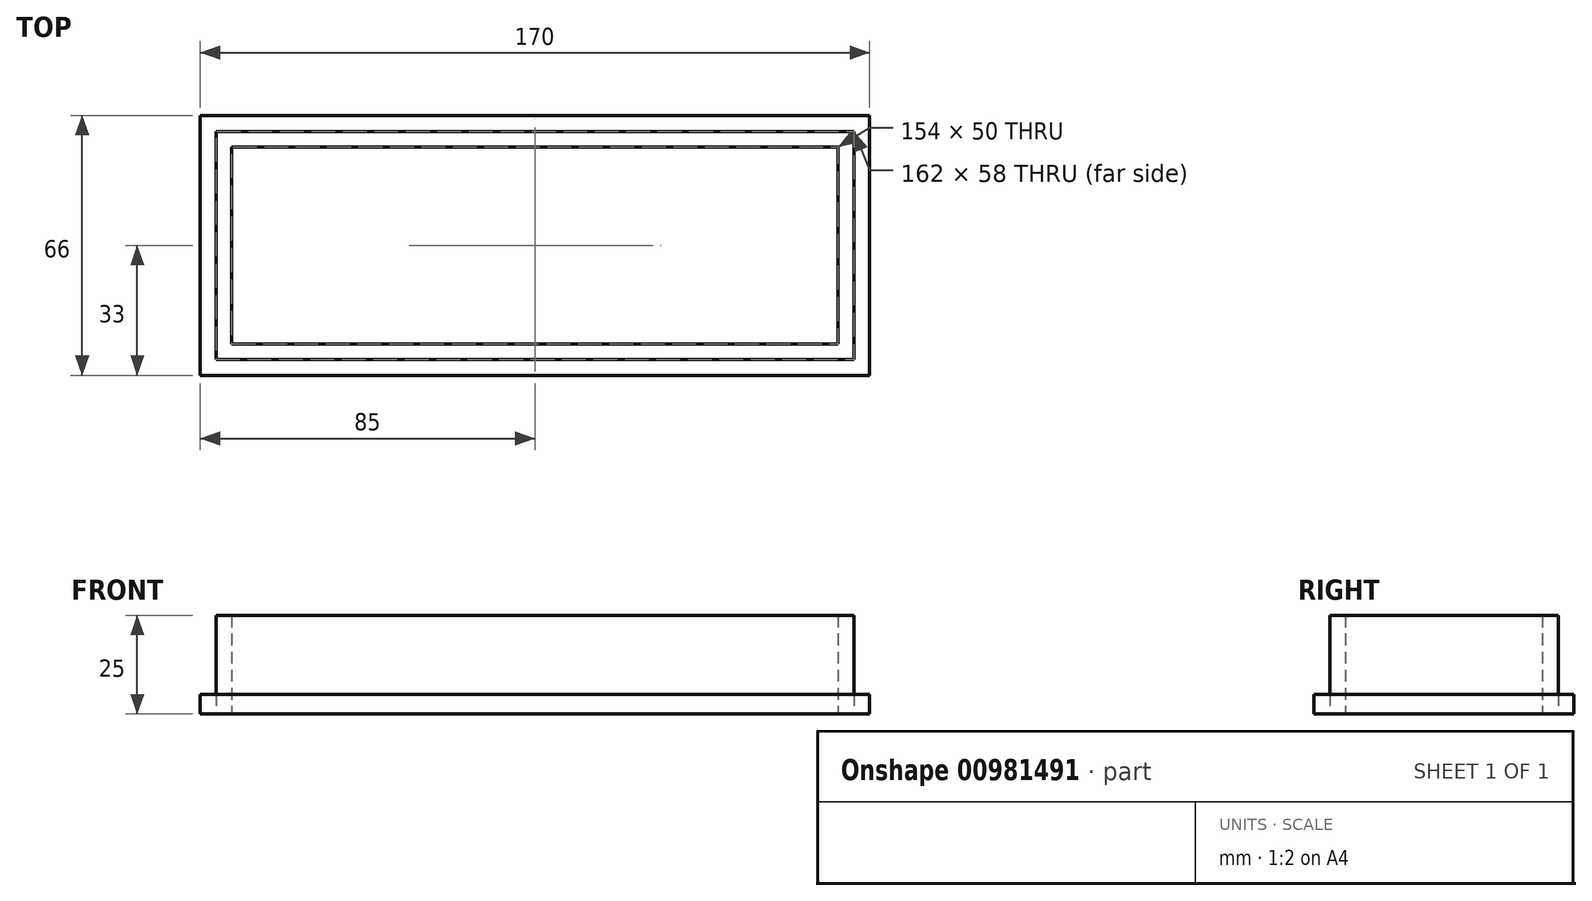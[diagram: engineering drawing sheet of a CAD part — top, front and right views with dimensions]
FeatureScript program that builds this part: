
annotation { "Feature Type Name" : "Feature", "Feature Type Description" : "" }
export const myFeature = defineFeature(function(context is Context, id is Id, definition is map)
    precondition{}
    {
        {
            var Q0;
            Q0=qCreatedBy(makeId("Top.planeOp"),FACE);
            var sketch = newSketch(context, id + "F0", { "sketchPlane" : qUnion([Q0])});
            skLineSegment(sketch, "E0.bottom", {"start": v(-85, 33) * mm, "end": v(85, 33) * mm});
            skLineSegment(sketch, "E0.top", {"start": v(-85, -33) * mm, "end": v(85, -33) * mm});
            skLineSegment(sketch, "E0.left", {"start": v(-85, 33) * mm, "end": v(-85, -33) * mm});
            skLineSegment(sketch, "E0.right", {"start": v(85, 33) * mm, "end": v(85, -33) * mm});
            skLineSegment(sketch, "E1.bottom", {"start": v(81, 29) * mm, "end": v(-81, 29) * mm});
            skLineSegment(sketch, "E1.top", {"start": v(81, -29) * mm, "end": v(-81, -29) * mm});
            skLineSegment(sketch, "E1.left", {"start": v(81, 29) * mm, "end": v(81, -29) * mm});
            skLineSegment(sketch, "E1.right", {"start": v(-81, 29) * mm, "end": v(-81, -29) * mm});
            skPoint(sketch, "E2", {"position": v(-81, 0) * mm});
            skPoint(sketch, "E3", {"position": v(-85, 0) * mm});
            skLineSegment(sketch, "E4", {"start": v(-142.94, 0) * mm, "end": v(129.94, 0) * mm, "construction": true});
            skLineSegment(sketch, "E5.bottom", {"start": v(-77, 25) * mm, "end": v(77, 25) * mm});
            skLineSegment(sketch, "E5.top", {"start": v(-77, -25) * mm, "end": v(77, -25) * mm});
            skLineSegment(sketch, "E5.left", {"start": v(-77, 25) * mm, "end": v(-77, -25) * mm});
            skLineSegment(sketch, "E5.right", {"start": v(77, 25) * mm, "end": v(77, -25) * mm});
            skPoint(sketch, "E6", {"position": v(-77, 0) * mm});
            skPoint(sketch, "E7", {"position": v(0, 25) * mm});
            skSolve(sketch);
        }
        {
            var Q0;
            Q0=makeQuery(id+"F0.imprint","IMPRINT",FACE,{"disambiguationData":[TD([[makeQuery(id+"F0.imprint","IMPRINT",EDGE,{"derivedFrom":sQuery(id+"F0.wireOp",EDGE,"E0.bottom")}),-1.0]])]});
            extrude(context, id + "F1", {"entities" : qUnion([Q0]), "depth" : 5 * mm, "offsetDistance" : 25 * mm});
        }
        {
            var Q0;
            Q0=makeQuery(id+"F0.imprint","IMPRINT",FACE,{"disambiguationData":[TD([[makeQuery(id+"F0.imprint","IMPRINT",EDGE,{"derivedFrom":sQuery(id+"F0.wireOp",EDGE,"E1.bottom")}),1.0]])]});
            extrude(context, id + "F2", {"entities" : qUnion([Q0]), "depth" : 25 * mm, "offsetDistance" : 25 * mm});
        }
    });
